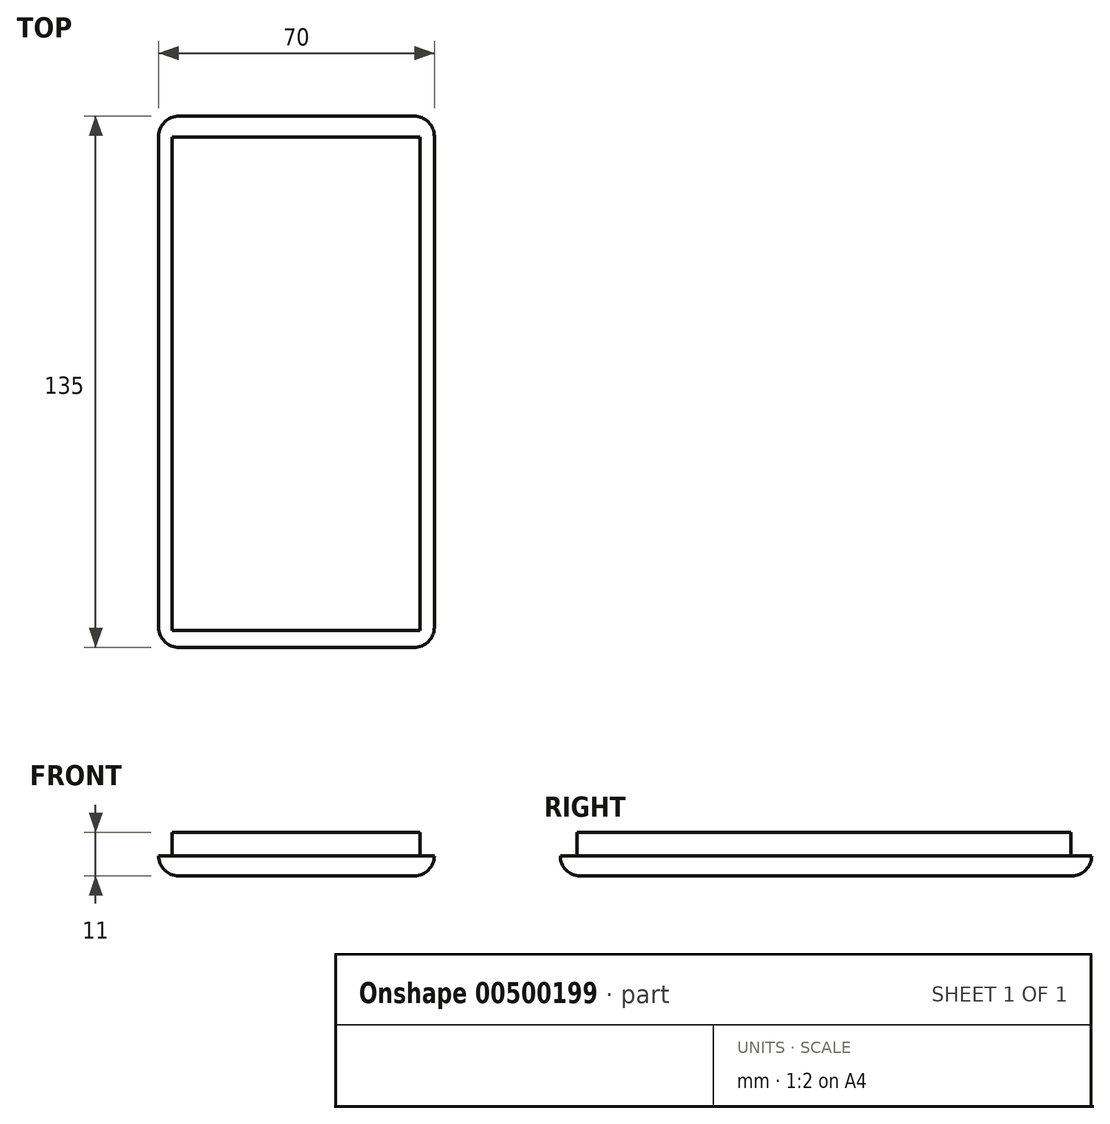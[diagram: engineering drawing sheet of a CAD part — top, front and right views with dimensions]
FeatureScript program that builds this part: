
annotation { "Feature Type Name" : "Feature", "Feature Type Description" : "" }
export const myFeature = defineFeature(function(context is Context, id is Id, definition is map)
    precondition{}
    {
        {
            var Q0;
            Q0=qCreatedBy(makeId("Top.planeOp"),FACE);
            var sketch = newSketch(context, id + "F0", { "sketchPlane" : qUnion([Q0])});
            skLineSegment(sketch, "E0.bottom", {"start": v(-68.11, 29.65) * mm, "end": v(11.89, 29.65) * mm});
            skLineSegment(sketch, "E0.top", {"start": v(-68.11, -115.35) * mm, "end": v(11.89, -115.35) * mm});
            skLineSegment(sketch, "E0.left", {"start": v(-68.11, 29.65) * mm, "end": v(-68.11, -115.35) * mm});
            skLineSegment(sketch, "E0.right", {"start": v(11.89, 29.65) * mm, "end": v(11.89, -115.35) * mm});
            skSolve(sketch);
        }
        {
            var Q0;
            Q0=makeQuery(id+"F0.imprint","IMPRINT",FACE,{"disambiguationData":[TD([[makeQuery(id+"F0.imprint","IMPRINT",EDGE,{"derivedFrom":sQuery(id+"F0.wireOp",EDGE,"E0.bottom")}),-1.0]])]});
            extrude(context, id + "F1", {"entities" : qUnion([Q0]), "depth" : 5 * mm});
        }
        {
            var Q0;
            Q0=makeQuery(id+"F1.opExtrude","SWEPT_EDGE",EDGE,{"disambiguationData":[OSD([sQuery(id+"F0.wireOp",EDGE,"E0.bottom"),sQuery(id+"F0.wireOp",EDGE,"E0.left")])]});
            var Q1;
            Q1=makeQuery(id+"F1.opExtrude","SWEPT_EDGE",EDGE,{"disambiguationData":[OSD([sQuery(id+"F0.wireOp",EDGE,"E0.top"),sQuery(id+"F0.wireOp",EDGE,"E0.left")])]});
            var Q2;
            Q2=makeQuery(id+"F1.opExtrude","SWEPT_EDGE",EDGE,{"disambiguationData":[OSD([sQuery(id+"F0.wireOp",EDGE,"E0.top"),sQuery(id+"F0.wireOp",EDGE,"E0.right")])]});
            var Q3;
            Q3=makeQuery(id+"F1.opExtrude","SWEPT_EDGE",EDGE,{"disambiguationData":[OSD([sQuery(id+"F0.wireOp",EDGE,"E0.bottom"),sQuery(id+"F0.wireOp",EDGE,"E0.right")])]});
            fillet(context, id + "F2", {"entities" : qUnion([Q0, Q1, Q2, Q3]), "radius" : 10.14 * mm, "tangentPropagation" : true, "allowEdgeOverflow" : false});
        }
        {
            var Q0;
            Q0=makeQuery(id+"F1.opExtrude","CAP_FACE",FACE,{"disambiguationData":[OSD([sQuery(id+"F0.wireOp",EDGE,"E0.bottom"),sQuery(id+"F0.wireOp",EDGE,"E0.top"),sQuery(id+"F0.wireOp",EDGE,"E0.left"),sQuery(id+"F0.wireOp",EDGE,"E0.right")])],"isStart":false});
            var sketch = newSketch(context, id + "F3", { "sketchPlane" : qUnion([Q0])});
            skLineSegment(sketch, "E1.bottom", {"start": v(-57.97, 19.51) * mm, "end": v(1.75, 19.51) * mm});
            skLineSegment(sketch, "E1.top", {"start": v(-57.97, -105.2) * mm, "end": v(1.75, -105.2) * mm});
            skLineSegment(sketch, "E1.left", {"start": v(-57.97, 19.51) * mm, "end": v(-57.97, -105.2) * mm});
            skLineSegment(sketch, "E1.right", {"start": v(1.75, 19.51) * mm, "end": v(1.75, -105.2) * mm});
            skSolve(sketch);
        }
        {
            var Q0;
            Q0=makeQuery(id+"F3.imprint","IMPRINT",FACE,{"disambiguationData":[TD([[makeQuery(id+"F3.imprint","IMPRINT",EDGE,{"derivedFrom":sQuery(id+"F3.wireOp",EDGE,"E1.bottom")}),-1.0]])]});
            extrude(context, id + "F4", {"entities" : qUnion([Q0]), "operationType" : NewBodyOperationType.ADD, "oppositeDirection" : true, "depth" : 2.1 * mm});
        }
        {
            var Q0;
            Q0=qCreatedBy(makeId("Top.planeOp"),FACE);
            var sketch = newSketch(context, id + "F5", { "sketchPlane" : qUnion([Q0])});
            skLineSegment(sketch, "E2.bottom", {"start": v(-59.67, 19.37) * mm, "end": v(3.24, 19.37) * mm});
            skLineSegment(sketch, "E2.top", {"start": v(-59.67, -106.09) * mm, "end": v(3.24, -106.09) * mm});
            skLineSegment(sketch, "E2.left", {"start": v(-59.67, 19.37) * mm, "end": v(-59.67, -106.09) * mm});
            skLineSegment(sketch, "E2.right", {"start": v(3.24, 19.37) * mm, "end": v(3.24, -106.09) * mm});
            skSolve(sketch);
        }
        {
            var Q0;
            Q0=makeQuery(id+"F1.opExtrude","CAP_FACE",FACE,{"disambiguationData":[OSD([sQuery(id+"F0.wireOp",EDGE,"E0.bottom"),sQuery(id+"F0.wireOp",EDGE,"E0.top"),sQuery(id+"F0.wireOp",EDGE,"E0.left"),sQuery(id+"F0.wireOp",EDGE,"E0.right")])],"isStart":false});
            chamfer(context, id + "F6", {"entities" : qUnion([Q0]), "width" : 5 * mm, "tangentPropagation" : true});
        }
        {
            var Q0;
            Q0=makeQuery(id+"F5.imprint","IMPRINT",FACE,{"disambiguationData":[TD([[makeQuery(id+"F5.imprint","IMPRINT",EDGE,{"derivedFrom":sQuery(id+"F5.wireOp",EDGE,"E2.bottom")}),-1.0]])]});
            extrude(context, id + "F7", {"entities" : qUnion([Q0]), "operationType" : NewBodyOperationType.ADD, "depth" : 11 * mm});
        }
        {
            var Q0;
            Q0=makeQuery(id+"F1.opExtrude","CAP_FACE",FACE,{"disambiguationData":[OSD([sQuery(id+"F0.wireOp",EDGE,"E0.bottom"),sQuery(id+"F0.wireOp",EDGE,"E0.top"),sQuery(id+"F0.wireOp",EDGE,"E0.left"),sQuery(id+"F0.wireOp",EDGE,"E0.right")])],"isStart":true});
            fillet(context, id + "F8", {"entities" : qUnion([Q0]), "radius" : 5 * mm, "tangentPropagation" : true, "allowEdgeOverflow" : false});
        }
    });
